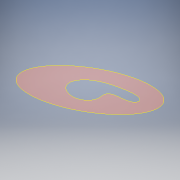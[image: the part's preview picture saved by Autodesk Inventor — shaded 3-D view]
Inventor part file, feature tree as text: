
AUTODESK INVENTOR PART (.ipt)
format: ipt  version: 2018 (Build 220112000, 112)  size: 94,208 bytes
history: native  units: mm
features: sketch x1, other x1, surface_op x1
ambient origin geometry x8: Origin, YZ Plane, XZ Plane, XY Plane, X Axis, Y Axis, Z Axis, Center Point
bodies: Body1 (feature_tree)
feature tree (3):
  sketch  "Sketch1"
  other  "Srf1"
  surface_op  "Boundary Patch1"
